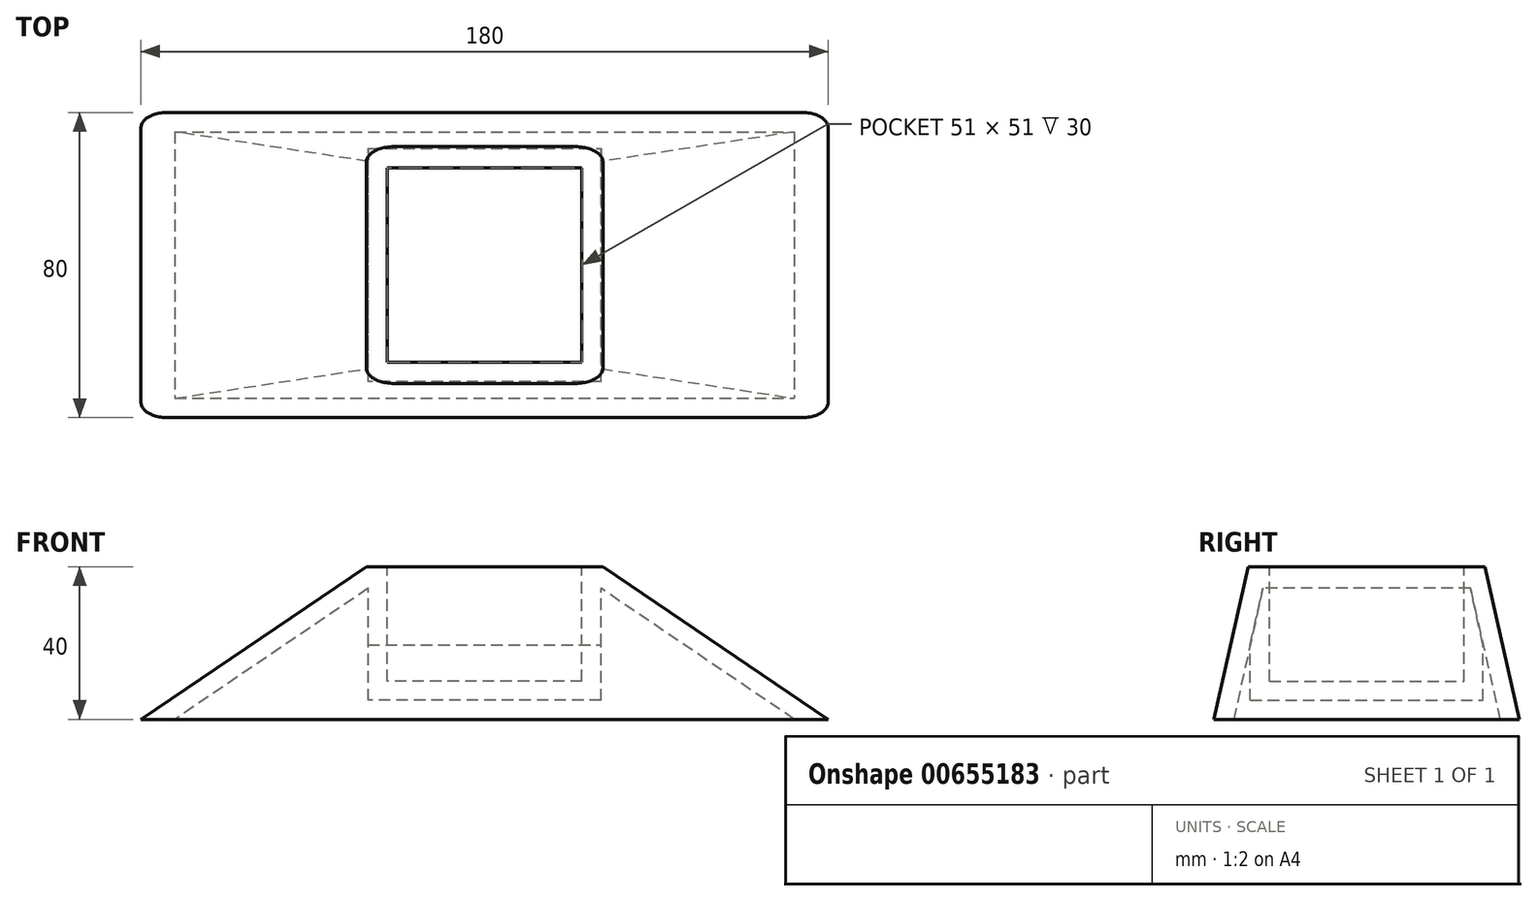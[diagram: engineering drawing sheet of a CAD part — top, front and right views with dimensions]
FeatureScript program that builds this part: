
annotation { "Feature Type Name" : "Feature", "Feature Type Description" : "" }
export const myFeature = defineFeature(function(context is Context, id is Id, definition is map)
    precondition{}
    {
        {
            var Q0;
            Q0=qCreatedBy(makeId("Top.planeOp"),FACE);
            var sketch = newSketch(context, id + "F0", { "sketchPlane" : qUnion([Q0])});
            skPoint(sketch, "E0", {"position": v(0, -25.5) * mm});
            skPoint(sketch, "E1", {"position": v(-25.5, 0) * mm});
            skLineSegment(sketch, "E2.bottom", {"start": v(-90, 40) * mm, "end": v(90, 40) * mm});
            skLineSegment(sketch, "E2.top", {"start": v(-90, -40) * mm, "end": v(90, -40) * mm});
            skLineSegment(sketch, "E2.left", {"start": v(-90, 40) * mm, "end": v(-90, -40) * mm});
            skLineSegment(sketch, "E2.right", {"start": v(90, 40) * mm, "end": v(90, -40) * mm});
            skPoint(sketch, "E3", {"position": v(-90, 0) * mm});
            skPoint(sketch, "E4", {"position": v(0, -40) * mm});
            skSolve(sketch);
        }
        {
            var Q0;
            Q0=qCreatedBy(makeId("Top.planeOp"),FACE);
            cPlane(context, id + "F1", {"entities" : qUnion([Q0]), "cplaneType" : CPlaneType.OFFSET, "offset" : 40 * mm, "width" : 150 * mm, "height" : 150 * mm});
        }
        {
            var Q0;
            Q0=qCreatedBy(id+"F1.planeOp",FACE);
            var sketch = newSketch(context, id + "F2", { "sketchPlane" : qUnion([Q0])});
            skLineSegment(sketch, "E5.0", {"start": v(31, 31) * mm, "end": v(-31, 31) * mm});
            skLineSegment(sketch, "E5.1", {"start": v(31, -31) * mm, "end": v(31, 31) * mm});
            skLineSegment(sketch, "E5.2", {"start": v(-31, -31) * mm, "end": v(31, -31) * mm});
            skLineSegment(sketch, "E5.3", {"start": v(-31, 31) * mm, "end": v(-31, -31) * mm});
            skSolve(sketch);
        }
        {
            var Q0;
            Q0=makeQuery(id+"F0.imprint","IMPRINT",FACE,{"disambiguationData":[TD([[makeQuery(id+"F0.imprint","IMPRINT",EDGE,{"derivedFrom":sQuery(id+"F0.wireOp",EDGE,"E2.bottom")}),-1.0]])]});
            var Q1;
            Q1=makeQuery(id+"F2.imprint","IMPRINT",FACE,{"disambiguationData":[TD([[makeQuery(id+"F2.imprint","IMPRINT",EDGE,{"derivedFrom":sQuery(id+"F2.wireOp",EDGE,"E5.0")}),1.0]])]});
            loft(context, id + "F3", {"sheetProfilesArray" : [{ "sheetProfileEntities" : qUnion([Q0]) }, { "sheetProfileEntities" : qUnion([Q1]) }]});
        }
        {
            var Q0;
            Q0=makeQuery(id+"F2.imprint","IMPRINT",FACE,{"disambiguationData":[TD([[makeQuery(id+"F2.imprint","IMPRINT",EDGE,{"derivedFrom":sQuery(id+"F2.wireOp",EDGE,"E5.0")}),1.0]])]});
            var sketch = newSketch(context, id + "F4", { "sketchPlane" : qUnion([Q0])});
            skLineSegment(sketch, "E6.bottom", {"start": v(25.5, -25.5) * mm, "end": v(-25.5, -25.5) * mm});
            skLineSegment(sketch, "E6.top", {"start": v(25.5, 25.5) * mm, "end": v(-25.5, 25.5) * mm});
            skLineSegment(sketch, "E6.left", {"start": v(25.5, -25.5) * mm, "end": v(25.5, 25.5) * mm});
            skLineSegment(sketch, "E6.right", {"start": v(-25.5, -25.5) * mm, "end": v(-25.5, 25.5) * mm});
            skPoint(sketch, "E7", {"position": v(25.5, 0) * mm});
            skPoint(sketch, "E8", {"position": v(0, 25.5) * mm});
            skPoint(sketch, "E9", {"position": v(0, 0) * mm});
            skSolve(sketch);
        }
        {
            var Q0;
            Q0=makeQuery(id+"F4.imprint","IMPRINT",FACE,{"disambiguationData":[TD([[makeQuery(id+"F4.imprint","IMPRINT",EDGE,{"derivedFrom":sQuery(id+"F4.wireOp",EDGE,"E6.bottom")}),-1.0]])]});
            extrude(context, id + "F5", {"entities" : qUnion([Q0]), "operationType" : NewBodyOperationType.REMOVE, "oppositeDirection" : true, "depth" : 30 * mm, "offsetDistance" : 25 * mm});
        }
        {
            var Q0;
            Q0=makeQuery(id+"F3.opLoft","CAP_FACE",FACE,{"disambiguationData":[OSD([makeQuery(id+"F0.imprint","IMPRINT",FACE,{"disambiguationData":[TD([[makeQuery(id+"F0.imprint","IMPRINT",EDGE,{"derivedFrom":sQuery(id+"F0.wireOp",EDGE,"E2.bottom")}),-1.0]])]})])],"isStart":true});
            shell(context, id + "F6", {"entities" : qUnion([Q0]), "thickness" : 5 * mm});
        }
        {
            var Q0;
            Q0=makeQuery(id+"F3.opLoft","SWEPT_EDGE",EDGE,{"disambiguationData":[OSD([sQuery(id+"F0.wireOp",EDGE,"E2.top"),sQuery(id+"F0.wireOp",EDGE,"E2.right"),sQuery(id+"F2.wireOp",EDGE,"E5.1"),sQuery(id+"F2.wireOp",EDGE,"E5.2")])]});
            var Q1;
            Q1=makeQuery(id+"F3.opLoft","SWEPT_EDGE",EDGE,{"disambiguationData":[OSD([sQuery(id+"F0.wireOp",EDGE,"E2.bottom"),sQuery(id+"F0.wireOp",EDGE,"E2.right"),sQuery(id+"F2.wireOp",EDGE,"E5.0"),sQuery(id+"F2.wireOp",EDGE,"E5.1")])]});
            var Q2;
            Q2=makeQuery(id+"F3.opLoft","SWEPT_EDGE",EDGE,{"disambiguationData":[OSD([sQuery(id+"F0.wireOp",EDGE,"E2.bottom"),sQuery(id+"F0.wireOp",EDGE,"E2.left"),sQuery(id+"F2.wireOp",EDGE,"E5.0"),sQuery(id+"F2.wireOp",EDGE,"E5.3")])]});
            var Q3;
            Q3=makeQuery(id+"F3.opLoft","SWEPT_EDGE",EDGE,{"disambiguationData":[OSD([sQuery(id+"F0.wireOp",EDGE,"E2.top"),sQuery(id+"F0.wireOp",EDGE,"E2.left"),sQuery(id+"F2.wireOp",EDGE,"E5.2"),sQuery(id+"F2.wireOp",EDGE,"E5.3")])]});
            fillet(context, id + "F7", {"entities" : qUnion([Q0, Q1, Q2, Q3]), "radius" : 5 * mm, "tangentPropagation" : true, "allowEdgeOverflow" : false});
        }
    });
